# Revit family: Наружный блок VRF системы 2
name_source: partatom
category: Mechanical Equipment
revit_build: Autodesk Revit 2016 (Build: 20150506_1715(x64)
units: mm (PartAtom-declared; Revit-internal decimal feet)

## family parameters
Cut with Voids When Loaded = No
Host = Face
Part Type = Normal
Room Calculation Point = No
Round Connector Dimension = Use Diameter
Shared = No

## types (6) — shared parameters
Default Elevation = 1219.2 mm  [stored 4 ft]
Высота = 1720 mm
Глубина = 750 mm  [stored 2.46063 ft]
Наименование = Наружный блок VRF-системы
Производитель = Electrolux
Таблица модель = Модель
Таблица наименование = Наименование
Таблица параметров = Таблица параметров
Таблица расход воздуха = Расход воздуха
Таблица тип хладагента = Тип хладагента
Таблица уровень звукового давления = Уровень звукового давления
Таблица электропитание = Электропитание
Тип хладогента = R410А
Фаза = 3
Частота сети = 50 Hz
Эл. питание(коннектор) = 380 V
Электропитание, (В) = 380

## per-type parameters (varying)
| type | SCOP, (кВт/кВт) | SEER, (кВт/кВт) | Артикул | Вес | Диаметр газовой трубы | Диаметр жидкостной трубы | Максимальная потребляемая мощность_Нагрев | Максимальная потребляемая мощность_Охлаждение | Максимальное кол-во подключаемых внутренних блоков, шт | Максимальный ток | Масса хладагента | Расход воздуха, (м.куб/ч) | Теплопроизводительность | Уровень звукового давления, (Дб(А)) | Холодопроизводительность | Ширина | Эффективная потребляемая мощность_Нагрев | Эффективная потребляемая мощность_Охлаждение |
| ESVMO-SF-224-7GiG | 9 | 8.6 | 1130346 | 224.00 kg | 19.05 mm  [stored 0.0625 ft] | 9.53 mm | 5.57 kW | 5.22 kW | 13 | 16 A | 8.00 kg | 9300 | 25.00 kW | 56 | 22.40 kW | 950 mm  [stored 3.1168 ft] | 3.34 kW | 3.13 kW |
| ESVMO-SF-280-7GiG | 8.4 | 7.7 | 1130347 | 225.00 kg | 22.2 mm  [stored 0.0728346 ft] | 9.53 mm | 7.48 kW | 7.29 kW | 16 | 17 A | 8.50 kg | 10200 | 31.50 kW | 57 | 28.00 kW | 950 mm  [stored 3.1168 ft] | 4.48 kW | 4.37 kW |
| ESVMO-SF-335-7GiG | 8 | 7.7 | 1130348 | 227.00 kg | 25.4 mm  [stored 0.0833333 ft] | 12.7 mm  [stored 0.0416667 ft] | 9.35 kW | 8.70 kW | 19 | 23 A | 9.90 kg | 10500 | 37.50 kW | 59 | 33.50 kW | 950 mm  [stored 3.1168 ft] | 5.61 kW | 5.22 kW |
| ESVMO-SF-400-7GiG | 8.2 | 7.3 | 1130350 | 312.00 kg | 25.4 mm  [stored 0.0833333 ft] | 12.7 mm  [stored 0.0416667 ft] | 10.98 kW | 10.99 kW | 23 | 28 A | 10.50 kg | 11700 | 45.00 kW | 59 | 40.00 kW | 1210 mm  [stored 3.96982 ft] | 6.58 kW | 6.59 kW |
| ESVMO-SF-450-7GiG | 8.1 | 6.9 | 1130352 | 315.00 kg | 28.6 mm  [stored 0.093832 ft] | 12.7 mm  [stored 0.0416667 ft] | 12.41 kW | 13.12 kW | 26 | 31 A | 10.50 kg | 11700 | 50.00 kW | 59 | 45.00 kW | 1210 mm  [stored 3.96982 ft] | 7.44 kW | 7.87 kW |
| ESVMO-SF-500-7GiG | 7.6 | 6.6 | 1130353 | 318.00 kg | 28.6 mm  [stored 0.093832 ft] | 15.88 mm  [stored 0.0520997 ft] | 14.70 kW | 15.11 kW | 26 | 33 A | 10.50 kg | 11700 | 56.00 kW | 60 | 50.00 kW | 1210 mm  [stored 3.96982 ft] | 8.82 kW | 9.06 kW |

note: column(s) folded — value = type name in every type: Модель

note: [stored X ft] marks values corroborated as IEEE doubles in the binary element streams (Revit-internal decimal feet)
